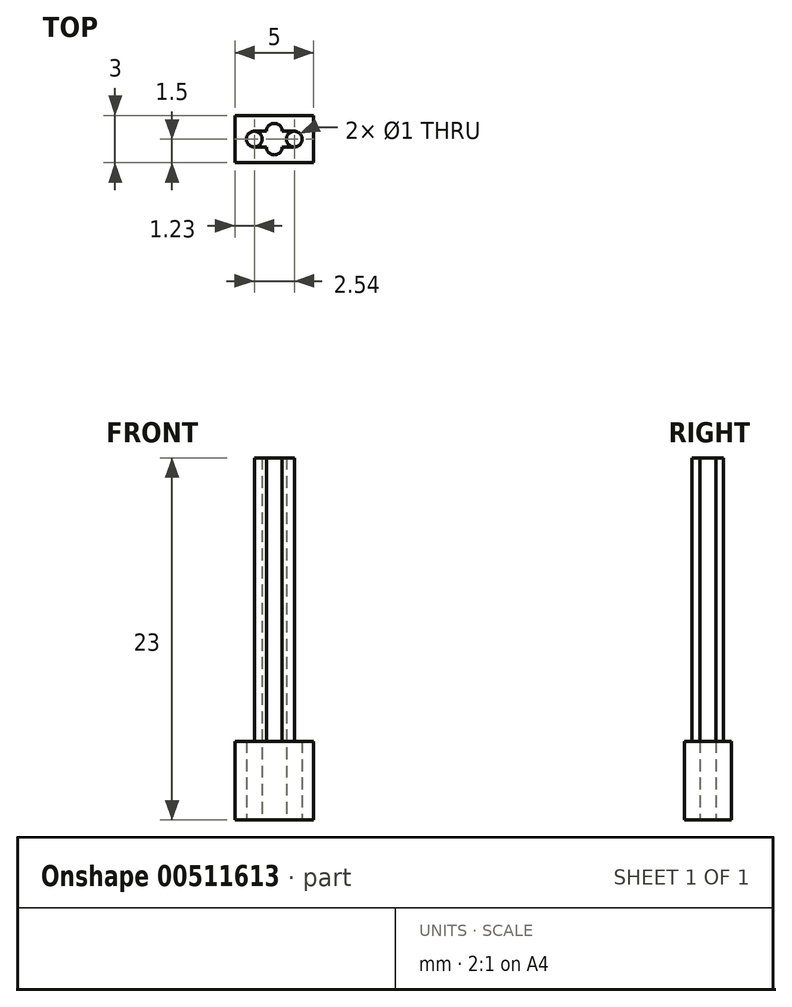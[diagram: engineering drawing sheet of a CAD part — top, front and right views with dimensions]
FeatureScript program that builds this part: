
annotation { "Feature Type Name" : "Feature", "Feature Type Description" : "" }
export const myFeature = defineFeature(function(context is Context, id is Id, definition is map)
    precondition{}
    {
        {
            var Q0;
            Q0=qCreatedBy(makeId("Top.planeOp"),FACE);
            var sketch = newSketch(context, id + "F0", { "sketchPlane" : qUnion([Q0])});
            skLineSegment(sketch, "E0.bottom", {"start": v(2.5, 1.5) * mm, "end": v(-2.5, 1.5) * mm});
            skLineSegment(sketch, "E0.top", {"start": v(2.5, -1.5) * mm, "end": v(-2.5, -1.5) * mm});
            skLineSegment(sketch, "E0.left", {"start": v(2.5, 1.5) * mm, "end": v(2.5, -1.5) * mm});
            skLineSegment(sketch, "E0.right", {"start": v(-2.5, 1.5) * mm, "end": v(-2.5, -1.5) * mm});
            skPoint(sketch, "E0.middle", {"position": v(0, 0) * mm});
            skLineSegment(sketch, "E1", {"start": v(0, 0) * mm, "end": v(1.27, 0) * mm});
            skCircle(sketch, "E2", {"center": v(1.27, 0) * mm, "radius": 0.5 * mm});
            skCircle(sketch, "E3.MirrorC", {"center": v(-1.27, 0) * mm, "radius": 0.5 * mm});
            skLineSegment(sketch, "E4", {"start": v(1.27, 0) * mm, "end": v(1.27, 0.5) * mm});
            skLineSegment(sketch, "E5", {"start": v(-1.27, 0) * mm, "end": v(-1.27, 0.5) * mm});
            skLineSegment(sketch, "E6", {"start": v(-1.27, 0.5) * mm, "end": v(1.27, 0.5) * mm});
            skLineSegment(sketch, "E7", {"start": v(-1.27, 0) * mm, "end": v(-1.27, -0.5) * mm});
            skLineSegment(sketch, "E8", {"start": v(-1.27, -0.5) * mm, "end": v(1.27, -0.5) * mm});
            skLineSegment(sketch, "E9", {"start": v(1.27, -0.5) * mm, "end": v(1.27, 0) * mm});
            skCircle(sketch, "E10", {"center": v(0, 0.5) * mm, "radius": 0.5 * mm});
            skCircle(sketch, "E11", {"center": v(0, -0.5) * mm, "radius": 0.5 * mm});
            skSolve(sketch);
        }
        {
            var Q0;
            Q0 = qSketchRegion(id + "F0", true);
            var Q1;
            {var subQ0=sQuery(id+"F0.wireOp",EDGE,"E10");var subQ1=sQuery(id+"F0.wireOp",EDGE,"E6");var subQ2=makeQuery(id+"F0.imprint","INTERSECT",VERTEX,{"disambiguationData":[OD(0.0)],"derivedFrom":[subQ1,subQ0]});Q1=makeQuery(id+"F0.imprint","IMPRINT",FACE,{"disambiguationData":[TD([[makeQuery(id+"F0.imprint","IMPRINT",EDGE,{"disambiguationData":[TD([[subQ2,-1.0]])],"derivedFrom":subQ1}),1.0]])]});}
            var Q2;
            {var subQ0=sQuery(id+"F0.wireOp",EDGE,"E10");var subQ1=sQuery(id+"F0.wireOp",EDGE,"E6");var subQ2=makeQuery(id+"F0.imprint","INTERSECT",VERTEX,{"disambiguationData":[OD(0.0)],"derivedFrom":[subQ1,subQ0]});Q2=makeQuery(id+"F0.imprint","IMPRINT",FACE,{"disambiguationData":[TD([[makeQuery(id+"F0.imprint","IMPRINT",EDGE,{"disambiguationData":[TD([[subQ2,-1.0]])],"derivedFrom":subQ1}),-1.0]])]});}
            var Q3;
            {var subQ0=sQuery(id+"F0.wireOp",EDGE,"E11");var subQ1=sQuery(id+"F0.wireOp",EDGE,"E8");var subQ2=makeQuery(id+"F0.imprint","INTERSECT",VERTEX,{"disambiguationData":[OD(0.0)],"derivedFrom":[subQ1,subQ0]});Q3=makeQuery(id+"F0.imprint","IMPRINT",FACE,{"disambiguationData":[TD([[makeQuery(id+"F0.imprint","IMPRINT",EDGE,{"disambiguationData":[TD([[subQ2,-1.0]])],"derivedFrom":subQ1}),1.0]])]});}
            var Q4;
            {var subQ0=sQuery(id+"F0.wireOp",EDGE,"E11");var subQ1=sQuery(id+"F0.wireOp",EDGE,"E8");var subQ2=makeQuery(id+"F0.imprint","INTERSECT",VERTEX,{"disambiguationData":[OD(0.0)],"derivedFrom":[subQ1,subQ0]});Q4=makeQuery(id+"F0.imprint","IMPRINT",FACE,{"disambiguationData":[TD([[makeQuery(id+"F0.imprint","IMPRINT",EDGE,{"disambiguationData":[TD([[subQ2,-1.0]])],"derivedFrom":subQ1}),-1.0]])]});}
            var Q5;
            {var subQ1=sQuery(id+"F0.wireOp",EDGE,"E10");var subQ3=sQuery(id+"F0.wireOp",EDGE,"E6");var subQ4=makeQuery(id+"F0.imprint","INTERSECT",VERTEX,{"disambiguationData":[OD(0.0)],"derivedFrom":[subQ3,subQ1]});Q5=makeQuery(id+"F0.imprint","IMPRINT",FACE,{"disambiguationData":[TD([[makeQuery(id+"F0.imprint","IMPRINT",EDGE,{"disambiguationData":[TD([[subQ4,1.0]])],"derivedFrom":subQ3}),-1.0]])]});}
            var Q6;
            {var subQ1=sQuery(id+"F0.wireOp",EDGE,"E1");var subQ3=sQuery(id+"F0.wireOp",EDGE,"E2");var subQ4=makeQuery(id+"F0.imprint","INTERSECT",VERTEX,{"derivedFrom":[subQ1,subQ3]});Q6=makeQuery(id+"F0.imprint","IMPRINT",FACE,{"disambiguationData":[TD([[makeQuery(id+"F0.imprint","IMPRINT",EDGE,{"disambiguationData":[TD([[subQ4,1.0]])],"derivedFrom":subQ1}),1.0]])]});}
            var Q7;
            {var subQ1=sQuery(id+"F0.wireOp",EDGE,"E1");var subQ3=sQuery(id+"F0.wireOp",EDGE,"E2");var subQ4=makeQuery(id+"F0.imprint","INTERSECT",VERTEX,{"derivedFrom":[subQ1,subQ3]});Q7=makeQuery(id+"F0.imprint","IMPRINT",FACE,{"disambiguationData":[TD([[makeQuery(id+"F0.imprint","IMPRINT",EDGE,{"disambiguationData":[TD([[subQ4,1.0]])],"derivedFrom":subQ1}),-1.0]])]});}
            extrude(context, id + "F1", {"entities" : qUnion([Q0, Q1, Q2, Q3, Q4, Q5, Q6, Q7]), "depth" : 5 * mm, "offsetDistance" : 25 * mm});
        }
        {
            var Q0;
            {var subQ1=sQuery(id+"F0.wireOp",EDGE,"E10");var subQ3=sQuery(id+"F0.wireOp",EDGE,"E6");var subQ4=makeQuery(id+"F0.imprint","INTERSECT",VERTEX,{"disambiguationData":[OD(0.0)],"derivedFrom":[subQ3,subQ1]});Q0=makeQuery(id+"F0.imprint","IMPRINT",FACE,{"disambiguationData":[TD([[makeQuery(id+"F0.imprint","IMPRINT",EDGE,{"disambiguationData":[TD([[subQ4,1.0]])],"derivedFrom":subQ3}),-1.0]])]});}
            var Q1;
            {var subQ0=sQuery(id+"F0.wireOp",EDGE,"E11");var subQ1=sQuery(id+"F0.wireOp",EDGE,"E8");var subQ2=makeQuery(id+"F0.imprint","INTERSECT",VERTEX,{"disambiguationData":[OD(0.0)],"derivedFrom":[subQ1,subQ0]});Q1=makeQuery(id+"F0.imprint","IMPRINT",FACE,{"disambiguationData":[TD([[makeQuery(id+"F0.imprint","IMPRINT",EDGE,{"disambiguationData":[TD([[subQ2,-1.0]])],"derivedFrom":subQ1}),1.0]])]});}
            var Q2;
            {var subQ0=sQuery(id+"F0.wireOp",EDGE,"E11");var subQ1=sQuery(id+"F0.wireOp",EDGE,"E8");var subQ2=makeQuery(id+"F0.imprint","INTERSECT",VERTEX,{"disambiguationData":[OD(0.0)],"derivedFrom":[subQ1,subQ0]});Q2=makeQuery(id+"F0.imprint","IMPRINT",FACE,{"disambiguationData":[TD([[makeQuery(id+"F0.imprint","IMPRINT",EDGE,{"disambiguationData":[TD([[subQ2,-1.0]])],"derivedFrom":subQ1}),-1.0]])]});}
            var Q3;
            {var subQ0=sQuery(id+"F0.wireOp",EDGE,"E10");var subQ1=sQuery(id+"F0.wireOp",EDGE,"E6");var subQ2=makeQuery(id+"F0.imprint","INTERSECT",VERTEX,{"disambiguationData":[OD(0.0)],"derivedFrom":[subQ1,subQ0]});Q3=makeQuery(id+"F0.imprint","IMPRINT",FACE,{"disambiguationData":[TD([[makeQuery(id+"F0.imprint","IMPRINT",EDGE,{"disambiguationData":[TD([[subQ2,-1.0]])],"derivedFrom":subQ1}),-1.0]])]});}
            var Q4;
            {var subQ0=sQuery(id+"F0.wireOp",EDGE,"E10");var subQ1=sQuery(id+"F0.wireOp",EDGE,"E6");var subQ2=makeQuery(id+"F0.imprint","INTERSECT",VERTEX,{"disambiguationData":[OD(0.0)],"derivedFrom":[subQ1,subQ0]});Q4=makeQuery(id+"F0.imprint","IMPRINT",FACE,{"disambiguationData":[TD([[makeQuery(id+"F0.imprint","IMPRINT",EDGE,{"disambiguationData":[TD([[subQ2,-1.0]])],"derivedFrom":subQ1}),1.0]])]});}
            var Q5;
            {var subQ1=sQuery(id+"F0.wireOp",EDGE,"E1");var subQ3=sQuery(id+"F0.wireOp",EDGE,"E2");var subQ4=makeQuery(id+"F0.imprint","INTERSECT",VERTEX,{"derivedFrom":[subQ1,subQ3]});Q5=makeQuery(id+"F0.imprint","IMPRINT",FACE,{"disambiguationData":[TD([[makeQuery(id+"F0.imprint","IMPRINT",EDGE,{"disambiguationData":[TD([[subQ4,1.0]])],"derivedFrom":subQ1}),1.0]])]});}
            var Q6;
            {var subQ1=sQuery(id+"F0.wireOp",EDGE,"E1");var subQ3=sQuery(id+"F0.wireOp",EDGE,"E2");var subQ4=makeQuery(id+"F0.imprint","INTERSECT",VERTEX,{"derivedFrom":[subQ1,subQ3]});Q6=makeQuery(id+"F0.imprint","IMPRINT",FACE,{"disambiguationData":[TD([[makeQuery(id+"F0.imprint","IMPRINT",EDGE,{"disambiguationData":[TD([[subQ4,1.0]])],"derivedFrom":subQ1}),-1.0]])]});}
            var Q7;
            {var subQ1=sQuery(id+"F0.wireOp",EDGE,"E2");var subQ3=sQuery(id+"F0.wireOp",EDGE,"E1");var subQ4=makeQuery(id+"F0.imprint","INTERSECT",VERTEX,{"derivedFrom":[subQ1,subQ3]});Q7=makeQuery(id+"F0.imprint","IMPRINT",FACE,{"disambiguationData":[TD([[makeQuery(id+"F0.imprint","IMPRINT",EDGE,{"disambiguationData":[TD([[subQ4,1.0]])],"derivedFrom":subQ1}),-1.0]])]});}
            var Q8;
            {var subQ1=sQuery(id+"F0.wireOp",EDGE,"E2");var subQ3=sQuery(id+"F0.wireOp",EDGE,"E1");var subQ4=makeQuery(id+"F0.imprint","INTERSECT",VERTEX,{"derivedFrom":[subQ1,subQ3]});Q8=makeQuery(id+"F0.imprint","IMPRINT",FACE,{"disambiguationData":[TD([[makeQuery(id+"F0.imprint","IMPRINT",EDGE,{"disambiguationData":[TD([[subQ4,-1.0]])],"derivedFrom":subQ1}),-1.0]])]});}
            extrude(context, id + "F2", {"entities" : qUnion([Q0, Q1, Q2, Q3, Q4, Q5, Q6, Q7, Q8]), "operationType" : NewBodyOperationType.ADD, "depth" : 23 * mm, "offsetDistance" : 25 * mm});
        }
    });
